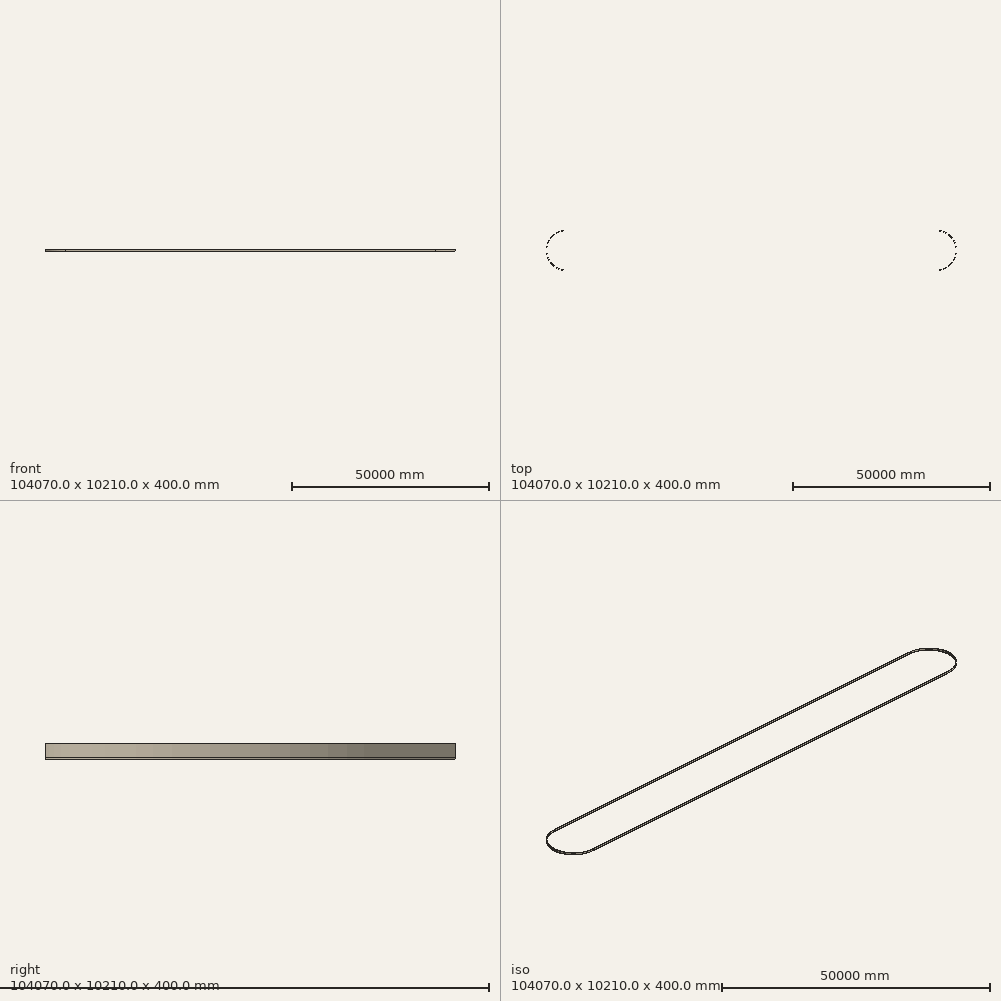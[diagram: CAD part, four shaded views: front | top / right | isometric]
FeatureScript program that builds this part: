
annotation { "Feature Type Name" : "Feature", "Feature Type Description" : "" }
export const myFeature = defineFeature(function(context is Context, id is Id, definition is map)
    precondition{}
    {
        {
            var Q0;
            Q0=qCreatedBy(makeId("Top.planeOp"),FACE);
            var sketch = newSketch(context, id + "F0", { "sketchPlane" : qUnion([Q0])});
            skLineSegment(sketch, "E0.bottom", {"start": v(0, 0) * mm, "end": v(0, 0) * mm});
            skLineSegment(sketch, "E0.top", {"start": v(0, 35) * mm, "end": v(0, 35) * mm});
            skLineSegment(sketch, "E0.left", {"start": v(0, 0) * mm, "end": v(0, 35) * mm});
            skLineSegment(sketch, "E0.right", {"start": v(0, 0) * mm, "end": v(0, 35) * mm});
            skLineSegment(sketch, "E1", {"start": v(0, 35) * mm, "end": v(-93860, 35) * mm});
            skLineSegment(sketch, "E2", {"start": v(0, 0) * mm, "end": v(0, -35) * mm});
            skLineSegment(sketch, "E3", {"start": v(0, -35) * mm, "end": v(-93860, -35) * mm});
            skLineSegment(sketch, "E4", {"start": v(-93860, 35) * mm, "end": v(-93860, -35) * mm});
            skLineSegment(sketch, "E5", {"start": v(-93860, 5035) * mm, "end": v(0, 5035) * mm});
            skLineSegment(sketch, "E6", {"start": v(-93860, 5105) * mm, "end": v(0, 5105) * mm});
            skLineSegment(sketch, "E7", {"start": v(-93860, -5035) * mm, "end": v(0, -5035) * mm});
            skLineSegment(sketch, "E8", {"start": v(-93860, -5105) * mm, "end": v(0, -5105) * mm});
            skArc(sketch, "E9", {"start": v(-93860, 5035) * mm, "mid": v(-98895, 0) * mm, "end": v(-93860, -5035) * mm});
            skArc(sketch, "E10", {"start": v(-93860, 5105) * mm, "mid": v(-98965, 0) * mm, "end": v(-93860, -5105) * mm});
            skArc(sketch, "E11", {"start": v(0, 5035) * mm, "mid": v(5035, 0) * mm, "end": v(0, -5035) * mm});
            skArc(sketch, "E12", {"start": v(0, 5105) * mm, "mid": v(5105, 0) * mm, "end": v(0, -5105) * mm});
            skSolve(sketch);
        }
        {
            var Q0;
            Q0=makeQuery(id+"F0.imprint","IMPRINT",FACE,{"disambiguationData":[TD([[makeQuery(id+"F0.imprint","IMPRINT",EDGE,{"derivedFrom":sQuery(id+"F0.wireOp",EDGE,"E0.right")}),1.0]])]});
            var Q1;
            Q1=makeQuery(id+"F0.imprint","IMPRINT",FACE,{"disambiguationData":[TD([[makeQuery(id+"F0.imprint","IMPRINT",EDGE,{"derivedFrom":sQuery(id+"F0.wireOp",EDGE,"E5")}),1.0]])]});
            extrude(context, id + "F1", {"entities" : qUnion([Q0, Q1]), "depth" : 350 * mm});
        }
        {
            var Q0;
            Q0=makeQuery(id+"F0.imprint","IMPRINT",FACE,{"disambiguationData":[TD([[makeQuery(id+"F0.imprint","IMPRINT",EDGE,{"derivedFrom":sQuery(id+"F0.wireOp",EDGE,"E0.right")}),-1.0]])]});
            var Q1;
            Q1=makeQuery(id+"F0.imprint","IMPRINT",FACE,{"disambiguationData":[TD([[makeQuery(id+"F0.imprint","IMPRINT",EDGE,{"derivedFrom":sQuery(id+"F0.wireOp",EDGE,"E5")}),1.0]])]});
            var Q2;
            Q2=makeQuery(id+"F0.imprint","IMPRINT",FACE,{"disambiguationData":[TD([[makeQuery(id+"F0.imprint","IMPRINT",EDGE,{"derivedFrom":sQuery(id+"F0.wireOp",EDGE,"E0.right")}),1.0]])]});
            extrude(context, id + "F2", {"entities" : qUnion([Q0, Q1, Q2]), "oppositeDirection" : true, "depth" : 50 * mm});
        }
    });
